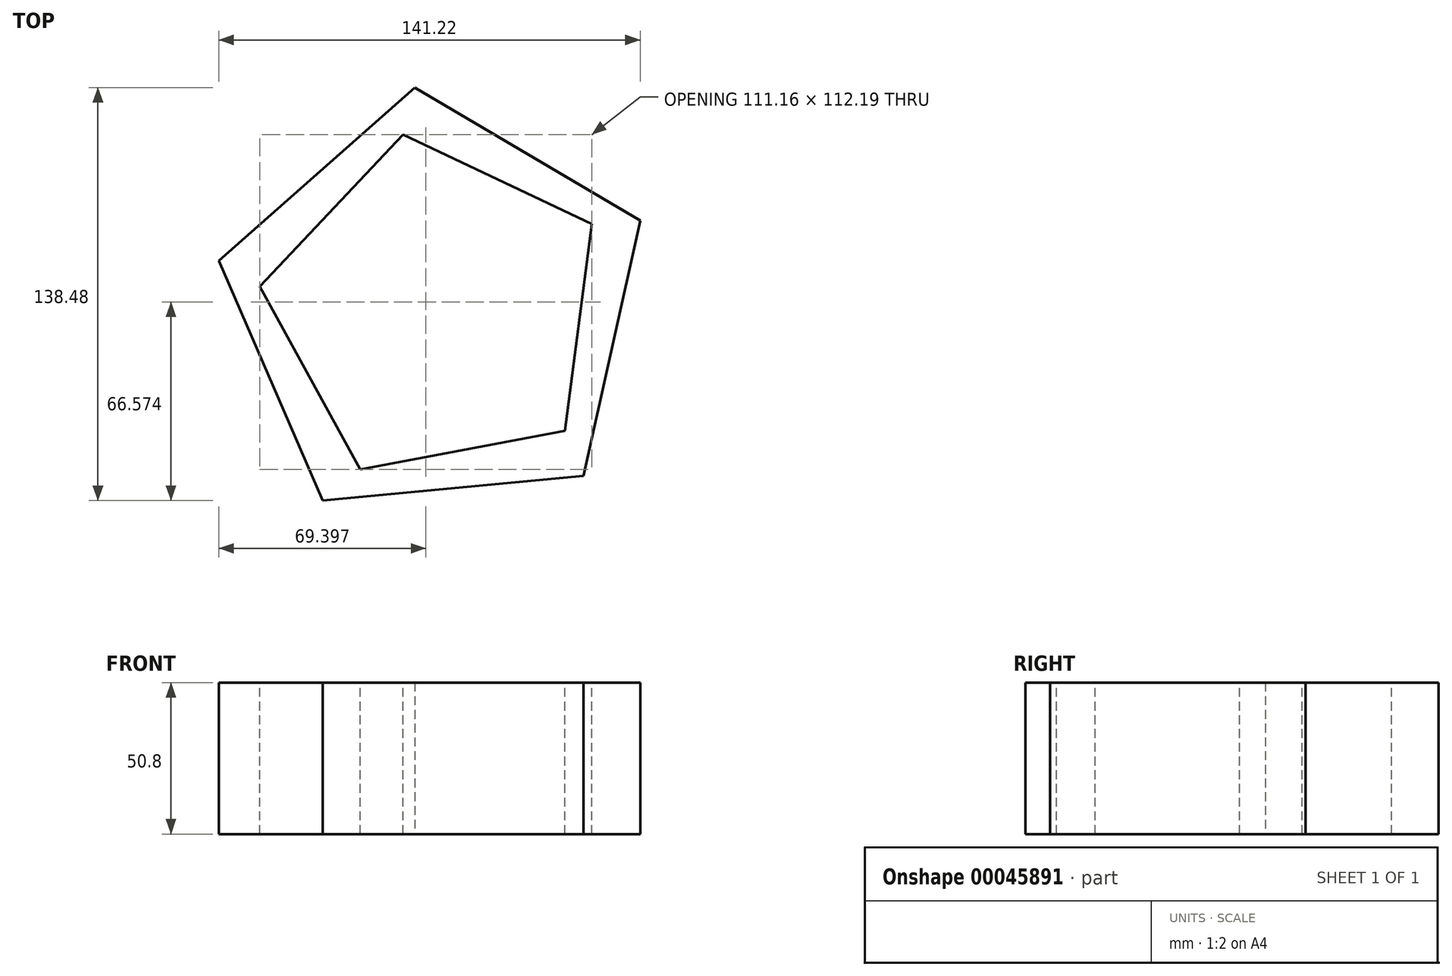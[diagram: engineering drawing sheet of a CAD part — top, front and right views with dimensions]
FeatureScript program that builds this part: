
annotation { "Feature Type Name" : "Feature", "Feature Type Description" : "" }
export const myFeature = defineFeature(function(context is Context, id is Id, definition is map)
    precondition{}
    {
        {
            var Q0;
            Q0=qCreatedBy(makeId("Top.planeOp"),FACE);
            var sketch = newSketch(context, id + "F0", { "sketchPlane" : qUnion([Q0])});
            skCircle(sketch, "E0.cCircle", {"center": v(0, 0) * mm, "radius": 60.34 * mm, "construction": true});
            skLineSegment(sketch, "E0.0", {"start": v(-7.08, 74.25) * mm, "end": v(68.42, 29.68) * mm});
            skLineSegment(sketch, "E0.1", {"start": v(68.42, 29.68) * mm, "end": v(49.37, -55.9) * mm});
            skLineSegment(sketch, "E0.2", {"start": v(49.37, -55.9) * mm, "end": v(-37.91, -64.23) * mm});
            skLineSegment(sketch, "E0.3", {"start": v(-37.91, -64.23) * mm, "end": v(-72.8, 16.2) * mm});
            skLineSegment(sketch, "E0.4", {"start": v(-72.8, 16.2) * mm, "end": v(-7.08, 74.25) * mm});
            skPoint(sketch, "E0.0.midPoint", {"position": v(30.67, 51.96) * mm});
            skSolve(sketch);
        }
        {
            var Q0;
            Q0=makeQuery(id+"F0.imprint","IMPRINT",FACE,{"disambiguationData":[TD([[makeQuery(id+"F0.imprint","IMPRINT",EDGE,{"derivedFrom":sQuery(id+"F0.wireOp",EDGE,"E0.0")}),-1.0]])]});
            extrude(context, id + "F1", {"entities" : qUnion([Q0]), "depth" : 25.4 * mm});
        }
        {
            var Q0;
            Q0=makeQuery(id+"F1.opExtrude","CAP_FACE",FACE,{"disambiguationData":[OSD([sQuery(id+"F0.wireOp",EDGE,"E0.0"),sQuery(id+"F0.wireOp",EDGE,"E0.1"),sQuery(id+"F0.wireOp",EDGE,"E0.2"),sQuery(id+"F0.wireOp",EDGE,"E0.3"),sQuery(id+"F0.wireOp",EDGE,"E0.4")])],"isStart":true});
            extrude(context, id + "F2", {"entities" : qUnion([Q0]), "operationType" : NewBodyOperationType.ADD, "depth" : 25.4 * mm});
        }
        {
            var Q0;
            Q0=makeQuery(id+"F1.opExtrude","CAP_FACE",FACE,{"disambiguationData":[OSD([sQuery(id+"F0.wireOp",EDGE,"E0.0"),sQuery(id+"F0.wireOp",EDGE,"E0.1"),sQuery(id+"F0.wireOp",EDGE,"E0.2"),sQuery(id+"F0.wireOp",EDGE,"E0.3"),sQuery(id+"F0.wireOp",EDGE,"E0.4")])],"isStart":false});
            var sketch = newSketch(context, id + "F3", { "sketchPlane" : qUnion([Q0])});
            skCircle(sketch, "E1.cCircle", {"center": v(0, 0) * mm, "radius": 48.11 * mm, "construction": true});
            skLineSegment(sketch, "E1.0", {"start": v(-11.01, 58.44) * mm, "end": v(52.18, 28.53) * mm});
            skLineSegment(sketch, "E1.1", {"start": v(52.18, 28.53) * mm, "end": v(43.26, -40.8) * mm});
            skLineSegment(sketch, "E1.2", {"start": v(43.26, -40.8) * mm, "end": v(-25.44, -53.75) * mm});
            skLineSegment(sketch, "E1.3", {"start": v(-25.44, -53.75) * mm, "end": v(-58.98, 7.59) * mm});
            skLineSegment(sketch, "E1.4", {"start": v(-58.98, 7.59) * mm, "end": v(-11.01, 58.44) * mm});
            skPoint(sketch, "E1.0.midPoint", {"position": v(20.58, 43.49) * mm});
            skSolve(sketch);
        }
        {
            var Q0;
            Q0 = qSketchRegion(id + "F3", true);
            extrude(context, id + "F4", {"entities" : qUnion([Q0]), "operationType" : NewBodyOperationType.REMOVE, "oppositeDirection" : true, "depth" : 25.4 * mm});
        }
        {
            var Q0;
            Q0=makeQuery(id+"F4.boolean.opBoolean","COPY",FACE,{"derivedFrom":makeQuery(id+"F4.opExtrude","CAP_FACE",FACE,{"disambiguationData":[OSD([sQuery(id+"F3.wireOp",EDGE,"E1.0"),sQuery(id+"F3.wireOp",EDGE,"E1.1"),sQuery(id+"F3.wireOp",EDGE,"E1.2"),sQuery(id+"F3.wireOp",EDGE,"E1.3"),sQuery(id+"F3.wireOp",EDGE,"E1.4")])],"isStart":false})});
            extrude(context, id + "F5", {"entities" : qUnion([Q0]), "operationType" : NewBodyOperationType.REMOVE, "oppositeDirection" : true, "depth" : 25.4 * mm});
        }
    });
